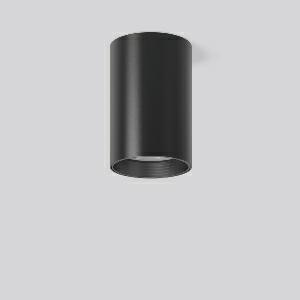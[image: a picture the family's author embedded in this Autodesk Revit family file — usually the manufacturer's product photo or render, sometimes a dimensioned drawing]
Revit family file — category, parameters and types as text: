
# Revit family: heledon_maxi_a_931229_003_3_fc50
name_source: partatom
category: Lighting Fixtures
units: mm (PartAtom-declared; Revit-internal decimal feet)

## family parameters
Cut with Voids When Loaded = No
Host = Face
Light Source = No
Part Type = Normal
Room Calculation Point = No
Round Connector Dimension = Use Diameter
Shared = No

## types (1)
- HELEDON maxi A (1 x LED Modul 935, 3650 lm, 3500)
    Apparent Load = 35 VA
    Approval mark = CE
    CIE Flux Codes = 96 100 100 100 100
    Color Rendering = 92
    Color Temperature = 3500
    Default Elevation = 1800 mm
    Description = Series: HELEDON maxi
Cylindrical surface-mounted downlight. Housing: die-cast aluminium, powder-coated. Internal ceiling frame polycarbonate with bayonet mounting. Black plastic ring and recessed LED to prevent glare from the side. Optical assembly with lens made of plastic (polycarbonate) for the best homogeneous light distribution - can be changed without tools. Best colour rendering index Ra>90. Suitable for Ceiling mounting. Easy installation with a separate ceiling frame with bayonet mounting and plug connection. Driver integrated. Connected via plug-in connector. High quality converter without flickering and stroboscopic effect. The following accessories can be mounted without use of tools: interchangeable lenses, decorative glasses, honeycomb louvre, clear and frosted diffusers, white interchangeable plastic ring. 
Colour: deep black, matt (RAL 9005)
Diameter: 123 mm
Height: 183 mm
Lamp: LED
Socket: without socket
Colour temperature: 3500K
Colour rendering index (CRI): 92
System power: 35 W
Rated luminous flux: 3650 lm
Luminous efficiency: 104 lm/W
Control gear: Regulated power supply
Protection class: I
Type of protection: IP 20
    Height = 183 mm
    Lamp = 1 x LED Modul 935
    Lamp Light Flux = 3650 lm
    Lamp count = 1
    Length = 123 mm
    Lifetime = 50000 h
    Luminous efficacy = 104 lm/W
    Manufacturer = RZB
    ModVariant = No
    Model = 931229.003.3
    Mounting Place = Ceiling
    Mounting Type = Surface mounted
    Number of Poles = 1
    OnlyDefault = Yes
    Power Factor = 1
    Product Name = HELEDON maxi A
    Product group = Surface mounted downlights
    ProductGroupID = 302
    Protection Class = Protection class I
    Protection Degree = IP 20
    RLX_Detail_Level = 1
    RLX_Emergency_Light_Flux = 0 lm
    RLX_Emergency_Type = 0
    RLX_Emergency_Type_DB = No
    RlxData = <blob elided: 97409 chars, md5=81b82997>
    Socket = socket
    Standby Power = 0 W
    System Light Flux = 3650 lm
    System Power = 35 W
    Type Comments = Product without accessories
    Type Image = 931193.003.jpg
    URL = http://relux.com
    VarID = ---
    Voltage = 230 V
    Voltage Range = 220-240 V
    Weight = 0.00 kg
    Width = 0 mm  [stored 0 ft]

note: [stored X ft] marks values corroborated as IEEE doubles in the binary element streams (Revit-internal decimal feet)

## geometry (parser evidence)
native form markers: Blend x4, Sweep x11
no freeform markers — native parametric forms only
